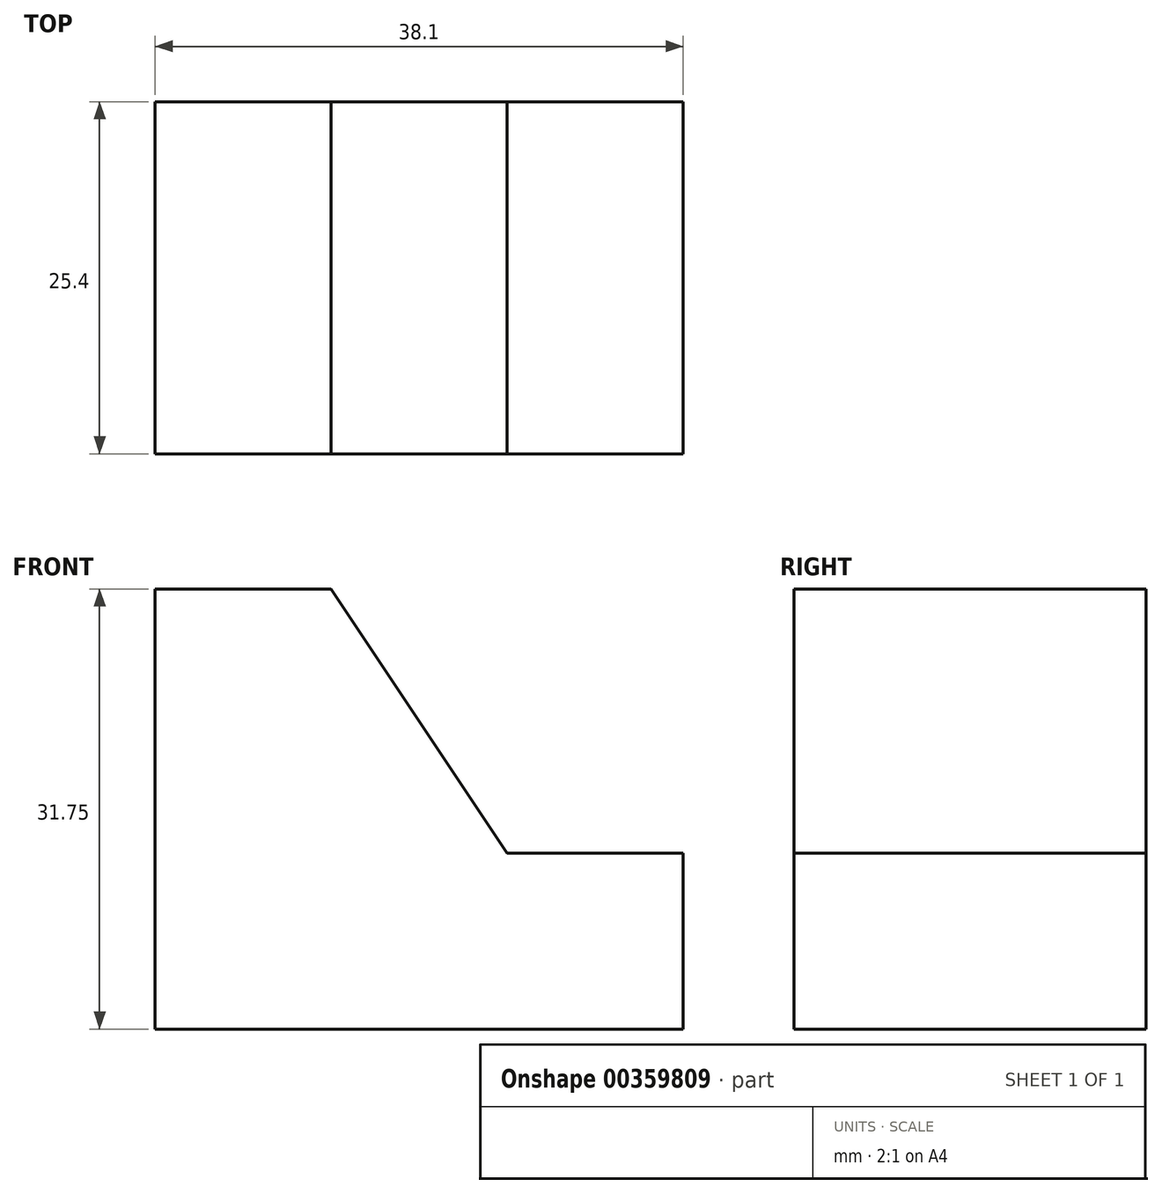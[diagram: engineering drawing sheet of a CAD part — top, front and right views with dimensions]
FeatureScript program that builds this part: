
annotation { "Feature Type Name" : "Feature", "Feature Type Description" : "" }
export const myFeature = defineFeature(function(context is Context, id is Id, definition is map)
    precondition{}
    {
        {
            var Q0;
            Q0=qCreatedBy(makeId("Front.planeOp"),FACE);
            var sketch = newSketch(context, id + "F0", { "sketchPlane" : qUnion([Q0])});
            skLineSegment(sketch, "E0.bottom", {"start": v(0, 0) * mm, "end": v(-38.1, 0) * mm});
            skLineSegment(sketch, "E0.top", {"start": v(0, 31.75) * mm, "end": v(-38.1, 31.75) * mm});
            skLineSegment(sketch, "E0.left", {"start": v(0, 0) * mm, "end": v(0, 31.75) * mm});
            skLineSegment(sketch, "E0.right", {"start": v(-38.1, 0) * mm, "end": v(-38.1, 31.75) * mm});
            skSolve(sketch);
        }
        {
            var Q0;
            Q0 = qSketchRegion(id + "F0", true);
            extrude(context, id + "F1", {"entities" : qUnion([Q0]), "depth" : 25.4 * mm});
        }
        {
            var Q0;
            Q0=makeQuery(id+"F1.opExtrude","CAP_FACE",FACE,{"disambiguationData":[OSD([sQuery(id+"F0.wireOp",EDGE,"E0.bottom"),sQuery(id+"F0.wireOp",EDGE,"E0.top"),sQuery(id+"F0.wireOp",EDGE,"E0.left"),sQuery(id+"F0.wireOp",EDGE,"E0.right")])],"isStart":false});
            var sketch = newSketch(context, id + "F2", { "sketchPlane" : qUnion([Q0])});
            skLineSegment(sketch, "E1", {"start": v(-12.7, 12.7) * mm, "end": v(0, 12.7) * mm});
            skLineSegment(sketch, "E2", {"start": v(-25.4, 31.75) * mm, "end": v(-12.7, 12.7) * mm});
            skSolve(sketch);
        }
        {
            var Q0;
            {var subQ0=sQuery(id+"F2.wireOp",EDGE,"E1");Q0=makeQuery(id+"F2.imprint","IMPRINT",FACE,{"disambiguationData":[TD([[makeQuery(id+"F2.imprint","IMPRINT",EDGE,{"derivedFrom":subQ0}),1.0]])]});}
            extrude(context, id + "F3", {"entities" : qUnion([Q0]), "operationType" : NewBodyOperationType.REMOVE, "oppositeDirection" : true, "depth" : 25.4 * mm});
        }
    });
